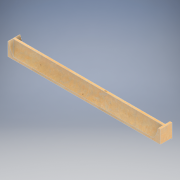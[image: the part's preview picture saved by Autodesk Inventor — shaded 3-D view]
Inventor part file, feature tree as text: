
AUTODESK INVENTOR PART (.ipt)
format: ipt  version: 2022.2 (Build 262287010, 287A)  size: 210,944 bytes
history: native  units: in
note: dims shown in document units (in); Inventor stores cm internally (conversion verified against a paired STEP export)
features: direct_edit x1, extrude x1, sketch x1, projected_geometry x1, revolve x1
ambient origin geometry x8: Origin, YZ Plane, XZ Plane, XY Plane, X Axis, Y Axis, Z Axis, Center Point
bodies: Solid1 (feature_tree), Body1 (feature_tree)
feature tree (5):
  direct_edit  "Direct Edit1"
  extrude  "Extrusion1"  Depth=0.375in TaperAngle=0.0deg
  sketch  "Sketch1"  dims[d0=180.0deg d1=0.375in d2=0.0in]
  projected_geometry  "Projected Loop1"
  revolve  "Rotate1"  [1 undecoded]
note: 1 required parameter value undecoded (feature->parameter linkage not recoverable at this tier; creation-order binding heuristic only, values carry confidence <= 0.55)
